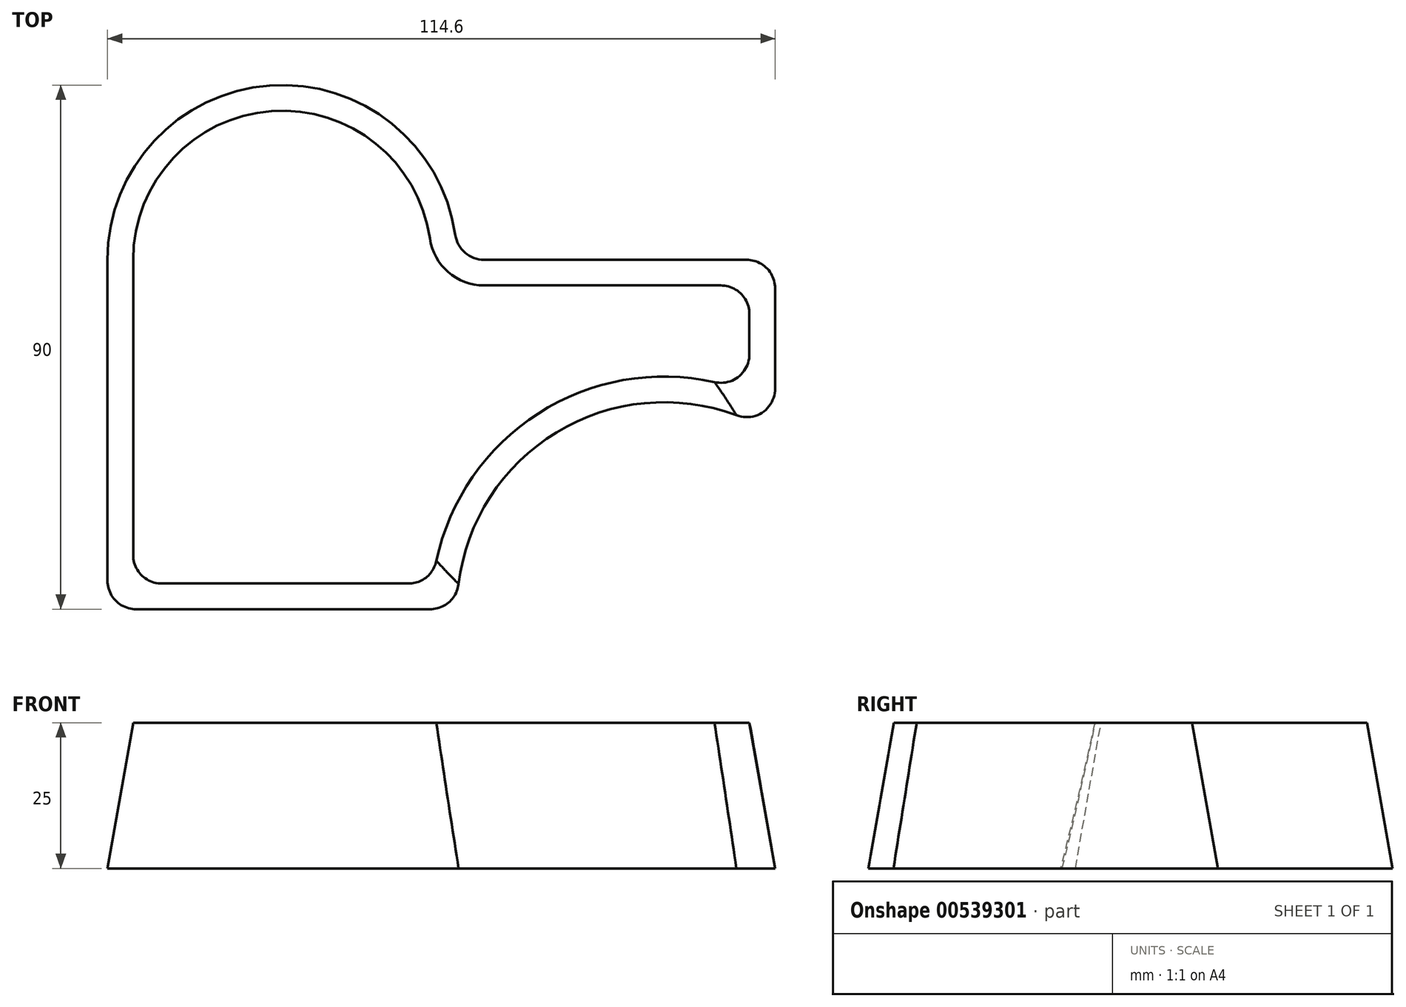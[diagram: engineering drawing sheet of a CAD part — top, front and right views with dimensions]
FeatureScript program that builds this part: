
annotation { "Feature Type Name" : "Feature", "Feature Type Description" : "" }
export const myFeature = defineFeature(function(context is Context, id is Id, definition is map)
    precondition{}
    {
        {
            var Q0;
            Q0=qCreatedBy(makeId("Top.planeOp"),FACE);
            var sketch = newSketch(context, id + "F0", { "sketchPlane" : qUnion([Q0])});
            skLineSegment(sketch, "E0.top", {"start": v(-114.6, -30) * mm, "end": v(-54.6, -30) * mm});
            skLineSegment(sketch, "E0.left", {"start": v(-114.6, 30) * mm, "end": v(-114.6, -30) * mm});
            skPoint(sketch, "E0.middle", {"position": v(-84.6, 0) * mm});
            skArc(sketch, "E1", {"start": v(-54.9, 34.29) * mm, "mid": v(-86.75, 59.92) * mm, "end": v(-114.6, 30) * mm});
            skLineSegment(sketch, "E2", {"start": v(-49.96, 30) * mm, "end": v(0, 30) * mm});
            skLineSegment(sketch, "E3", {"start": v(0, 30) * mm, "end": v(0, 0) * mm});
            skArc(sketch, "E4", {"start": v(0, 0) * mm, "mid": v(-36.17, 1.15) * mm, "end": v(-54.6, -30) * mm});
            skPoint(sketch, "E5.visualSharp", {"position": v(-54.6, 30) * mm});
            skArc(sketch, "E5.filletArc", {"start": v(-54.9, 34.29) * mm, "mid": v(-53.23, 31.22) * mm, "end": v(-49.96, 30) * mm});
            skSolve(sketch);
        }
        {
            var Q0;
            Q0=makeQuery(id+"F0.imprint","IMPRINT",FACE,{"disambiguationData":[TD([[makeQuery(id+"F0.imprint","IMPRINT",EDGE,{"derivedFrom":sQuery(id+"F0.wireOp",EDGE,"E0.top")}),1.0]])]});
            extrude(context, id + "F1", {"entities" : qUnion([Q0]), "depth" : 25 * mm, "offsetDistance" : 25 * mm, "hasDraft" : true, "draftAngle" : 10 * degree, "draftPullDirection" : true});
        }
        {
            var Q0;
            Q0=makeQuery(id+"F1.opExtrude","SWEPT_EDGE",EDGE,{"disambiguationData":[OSD([sQuery(id+"F0.wireOp",EDGE,"E0.top"),sQuery(id+"F0.wireOp",EDGE,"E0.left")])]});
            var Q1;
            Q1=makeQuery(id+"F1.opExtrude","SWEPT_EDGE",EDGE,{"disambiguationData":[OSD([sQuery(id+"F0.wireOp",EDGE,"E0.top"),sQuery(id+"F0.wireOp",EDGE,"E4")])]});
            var Q2;
            Q2=makeQuery(id+"F1.opExtrude","SWEPT_EDGE",EDGE,{"disambiguationData":[OSD([sQuery(id+"F0.wireOp",EDGE,"E3"),sQuery(id+"F0.wireOp",EDGE,"E4")])]});
            var Q3;
            Q3=makeQuery(id+"F1.opExtrude","SWEPT_EDGE",EDGE,{"disambiguationData":[OSD([sQuery(id+"F0.wireOp",EDGE,"E2"),sQuery(id+"F0.wireOp",EDGE,"E3")])]});
            fillet(context, id + "F2", {"entities" : qUnion([Q0, Q1, Q2, Q3]), "radius" : 5 * mm, "tangentPropagation" : true, "allowEdgeOverflow" : false});
        }
    });
